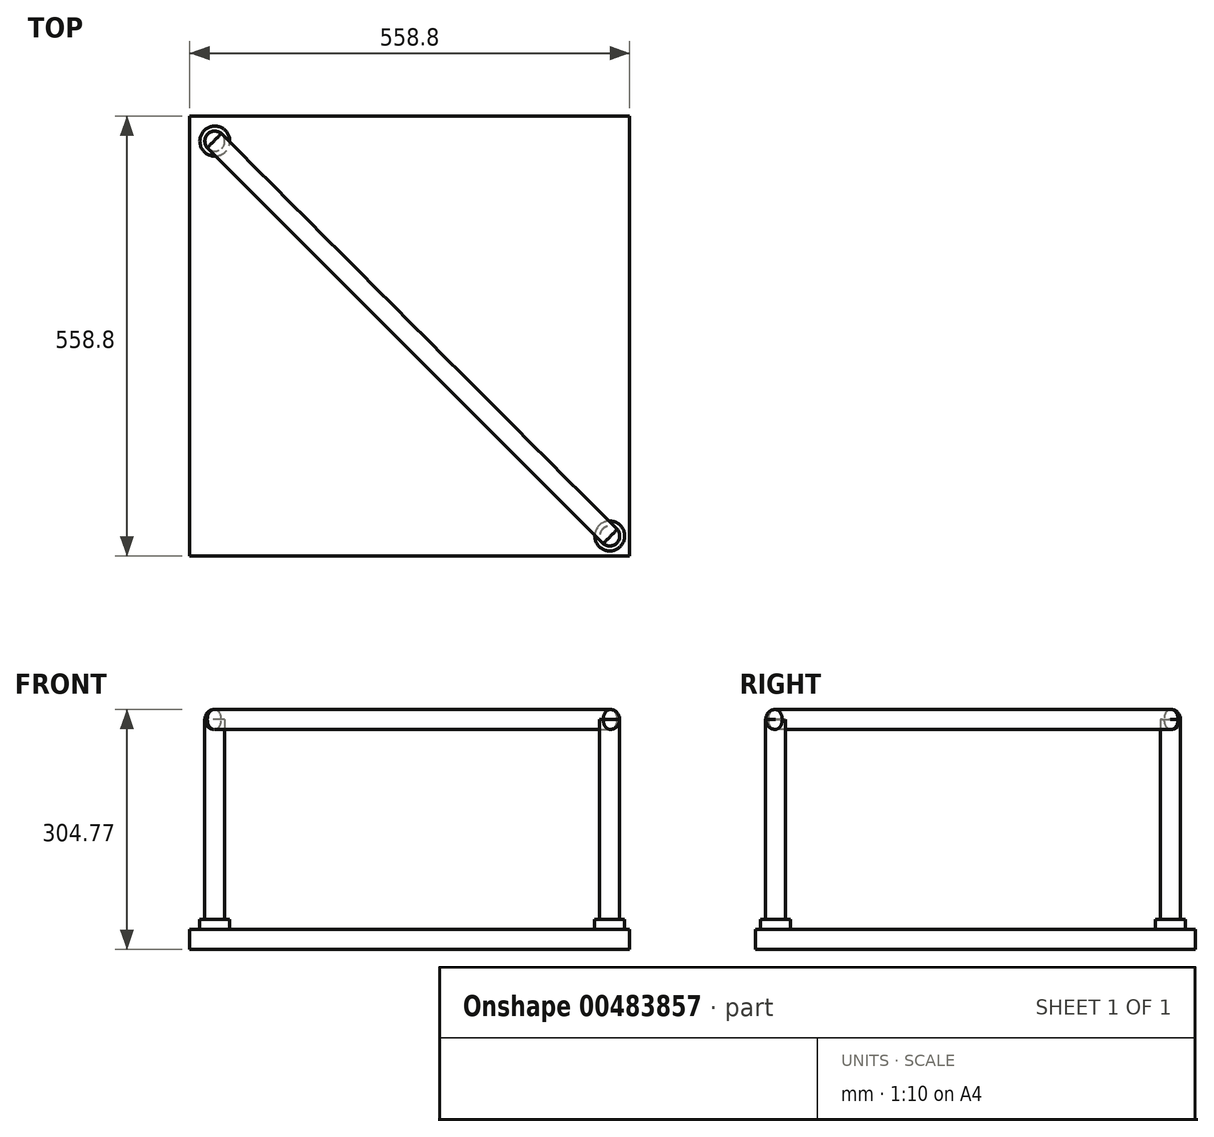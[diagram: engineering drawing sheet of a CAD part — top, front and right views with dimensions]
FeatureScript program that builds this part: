
annotation { "Feature Type Name" : "Feature", "Feature Type Description" : "" }
export const myFeature = defineFeature(function(context is Context, id is Id, definition is map)
    precondition{}
    {
        {
            var Q0;
            Q0=qCreatedBy(makeId("Top.planeOp"),FACE);
            var sketch = newSketch(context, id + "F0", { "sketchPlane" : qUnion([Q0])});
            skLineSegment(sketch, "E0.bottom", {"start": v(-558.8, 558.8) * mm, "end": v(0, 558.8) * mm});
            skLineSegment(sketch, "E0.top", {"start": v(-558.8, 0) * mm, "end": v(0, 0) * mm});
            skLineSegment(sketch, "E0.left", {"start": v(-558.8, 558.8) * mm, "end": v(-558.8, 0) * mm});
            skLineSegment(sketch, "E0.right", {"start": v(0, 558.8) * mm, "end": v(0, 0) * mm});
            skSolve(sketch);
        }
        {
            var Q0;
            Q0 = qSketchRegion(id + "F0", true);
            extrude(context, id + "F1", {"entities" : qUnion([Q0]), "depth" : 25.4 * mm});
        }
        {
            var Q0;
            Q0=qCreatedBy(makeId("Front.planeOp"),FACE);
            cPlane(context, id + "F2", {"entities" : qUnion([Q0]), "cplaneType" : CPlaneType.OFFSET, "offset" : 25.4 * mm, "oppositeDirection" : true, "width" : 152.4 * mm, "height" : 152.4 * mm});
        }
        {
            var Q0;
            Q0=qCreatedBy(id+"F2.planeOp",FACE);
            var sketch = newSketch(context, id + "F3", { "sketchPlane" : qUnion([Q0])});
            skLineSegment(sketch, "E1.bottom", {"start": v(-44.45, 38.1) * mm, "end": v(-6.35, 38.1) * mm});
            skLineSegment(sketch, "E1.top", {"start": v(-44.45, 25.4) * mm, "end": v(-6.35, 25.4) * mm});
            skLineSegment(sketch, "E1.left", {"start": v(-44.45, 38.1) * mm, "end": v(-44.45, 25.4) * mm});
            skLineSegment(sketch, "E1.right", {"start": v(-6.35, 38.1) * mm, "end": v(-6.35, 25.4) * mm});
            skLineSegment(sketch, "E2.bottom", {"start": v(-38.1, 38.1) * mm, "end": v(-12.7, 38.1) * mm});
            skLineSegment(sketch, "E2.top", {"start": v(-38.1, 50.8) * mm, "end": v(-12.7, 50.8) * mm});
            skLineSegment(sketch, "E2.left", {"start": v(-38.1, 38.1) * mm, "end": v(-38.1, 50.8) * mm});
            skLineSegment(sketch, "E2.right", {"start": v(-12.7, 38.1) * mm, "end": v(-12.7, 50.8) * mm});
            skLineSegment(sketch, "E3", {"start": v(-25.4, 50.8) * mm, "end": v(-25.4, 25.4) * mm});
            skSolve(sketch);
        }
        {
            var Q0;
            {var subQ0=sQuery(id+"F3.wireOp",EDGE,"E2.right");Q0=makeQuery(id+"F3.imprint","IMPRINT",FACE,{"disambiguationData":[TD([[makeQuery(id+"F3.imprint","IMPRINT",EDGE,{"derivedFrom":subQ0}),1.0]])]});}
            var Q1;
            {var subQ5=sQuery(id+"F3.wireOp",EDGE,"E1.right");Q1=makeQuery(id+"F3.imprint","IMPRINT",FACE,{"disambiguationData":[TD([[makeQuery(id+"F3.imprint","IMPRINT",EDGE,{"derivedFrom":subQ5}),-1.0]])]});}
            var Q2;
            Q2=sQuery(id+"F3.wireOp",EDGE,"E3");
            revolve(context, id + "F4", {"operationType" : NewBodyOperationType.ADD, "entities" : qUnion([Q0, Q1]), "axis" : qUnion([Q2]), "revolveType" : RevolveType.FULL});
        }
        {
            var Q0;
            Q0=makeQuery(id+"F1.opExtrude","CAP_FACE",FACE,{"disambiguationData":[OSD([sQuery(id+"F0.wireOp",EDGE,"E0.bottom"),sQuery(id+"F0.wireOp",EDGE,"E0.top"),sQuery(id+"F0.wireOp",EDGE,"E0.left"),sQuery(id+"F0.wireOp",EDGE,"E0.right")])],"isStart":false});
            var sketch = newSketch(context, id + "F5", { "sketchPlane" : qUnion([Q0])});
            skCircle(sketch, "E4", {"center": v(-527.05, 527.05) * mm, "radius": 19.05 * mm});
            skCircle(sketch, "E5", {"center": v(-527.05, 527.05) * mm, "radius": 12.7 * mm});
            skSolve(sketch);
        }
        {
            var Q0;
            Q0=makeQuery(id+"F5.imprint","IMPRINT",FACE,{"disambiguationData":[TD([[makeQuery(id+"F5.imprint","IMPRINT",EDGE,{"derivedFrom":sQuery(id+"F5.wireOp",EDGE,"E4")}),1.0]])]});
            extrude(context, id + "F6", {"entities" : qUnion([Q0]), "operationType" : NewBodyOperationType.ADD, "depth" : 12.7 * mm});
        }
        {
            var Q0;
            Q0=makeQuery(id+"F6.boolean.opBoolean","SPLIT",FACE,{"disambiguationData":[TD([makeQuery(id+"F6.opExtrude","SWEPT_FACE",FACE,{"disambiguationData":[OSD([sQuery(id+"F5.wireOp",EDGE,"E5")])]})])],"derivedFrom":makeQuery(id+"F1.opExtrude","CAP_FACE",FACE,{"disambiguationData":[OSD([sQuery(id+"F0.wireOp",EDGE,"E0.bottom"),sQuery(id+"F0.wireOp",EDGE,"E0.top"),sQuery(id+"F0.wireOp",EDGE,"E0.left"),sQuery(id+"F0.wireOp",EDGE,"E0.right")])],"isStart":false})});
            extrude(context, id + "F7", {"entities" : qUnion([Q0]), "operationType" : NewBodyOperationType.ADD, "depth" : 266.7 * mm});
        }
        {
            var Q0;
            Q0=makeQuery(id+"F4.opRevolve","SWEPT_FACE",FACE,{"disambiguationData":[OSD([sQuery(id+"F3.wireOp",EDGE,"E2.top")])]});
            extrude(context, id + "F8", {"entities" : qUnion([Q0]), "operationType" : NewBodyOperationType.ADD, "depth" : 241.3 * mm});
        }
        {
            var Q0;
            Q0=makeQuery(id+"F8.opExtrude","CAP_FACE",FACE,{"disambiguationData":[OSD([sQuery(id+"F3.wireOp",EDGE,"E2.top")])],"isStart":false});
            cPlane(context, id + "F9", {"entities" : qUnion([Q0]), "cplaneType" : CPlaneType.OFFSET, "offset" : 0 * mm, "width" : 152.4 * mm, "height" : 152.4 * mm});
        }
        {
            var Q0;
            Q0=qCreatedBy(id+"F9.planeOp",FACE);
            var sketch = newSketch(context, id + "F10", { "sketchPlane" : qUnion([Q0])});
            skCircle(sketch, "E6", {"center": v(-25.4, 25.4) * mm, "radius": 12.7 * mm});
            skCircle(sketch, "E7", {"center": v(-527.05, 527.05) * mm, "radius": 12.7 * mm});
            skLineSegment(sketch, "E8", {"start": v(-16.42, 16.42) * mm, "end": v(-536.03, 536.03) * mm});
            skLineSegment(sketch, "E9", {"start": v(-15.82, 33.74) * mm, "end": v(-518.71, 536.63) * mm});
            skLineSegment(sketch, "E10", {"start": v(-536.63, 518.71) * mm, "end": v(-33.74, 15.82) * mm});
            skSolve(sketch);
        }
        {
            var Q0;
            {var subQ0=sQuery(id+"F10.wireOp",EDGE,"E10");var subQ1=sQuery(id+"F10.wireOp",EDGE,"E6");var subQ2=makeQuery(id+"F10.imprint","INTERSECT",VERTEX,{"disambiguationData":[OD(1.0)],"derivedFrom":[subQ1,subQ0]});Q0=makeQuery(id+"F10.imprint","IMPRINT",FACE,{"disambiguationData":[TD([[makeQuery(id+"F10.imprint","IMPRINT",EDGE,{"disambiguationData":[TD([[subQ2,1.0]])],"derivedFrom":subQ1}),-1.0]])]});}
            var Q1;
            {var subQ0=sQuery(id+"F10.wireOp",EDGE,"E8");var subQ1=sQuery(id+"F10.wireOp",EDGE,"E7");var subQ2=makeQuery(id+"F10.imprint","INTERSECT",VERTEX,{"disambiguationData":[OD(0.0)],"derivedFrom":[subQ1,subQ0]});Q1=makeQuery(id+"F10.imprint","IMPRINT",FACE,{"disambiguationData":[TD([[makeQuery(id+"F10.imprint","IMPRINT",EDGE,{"disambiguationData":[TD([[subQ2,-1.0]])],"derivedFrom":subQ1}),1.0]])]});}
            var Q2;
            {var subQ0=sQuery(id+"F10.wireOp",EDGE,"E10");var subQ1=sQuery(id+"F10.wireOp",EDGE,"E6");var subQ2=makeQuery(id+"F10.imprint","INTERSECT",VERTEX,{"disambiguationData":[OD(1.0)],"derivedFrom":[subQ1,subQ0]});Q2=makeQuery(id+"F10.imprint","IMPRINT",FACE,{"disambiguationData":[TD([[makeQuery(id+"F10.imprint","IMPRINT",EDGE,{"disambiguationData":[TD([[subQ2,1.0]])],"derivedFrom":subQ1}),1.0]])]});}
            var Q3;
            Q3=sQuery(id+"F10.wireOp",EDGE,"E8");
            revolve(context, id + "F11", {"entities" : qUnion([Q0, Q1, Q2]), "axis" : qUnion([Q3]), "revolveType" : RevolveType.FULL});
        }
    });
